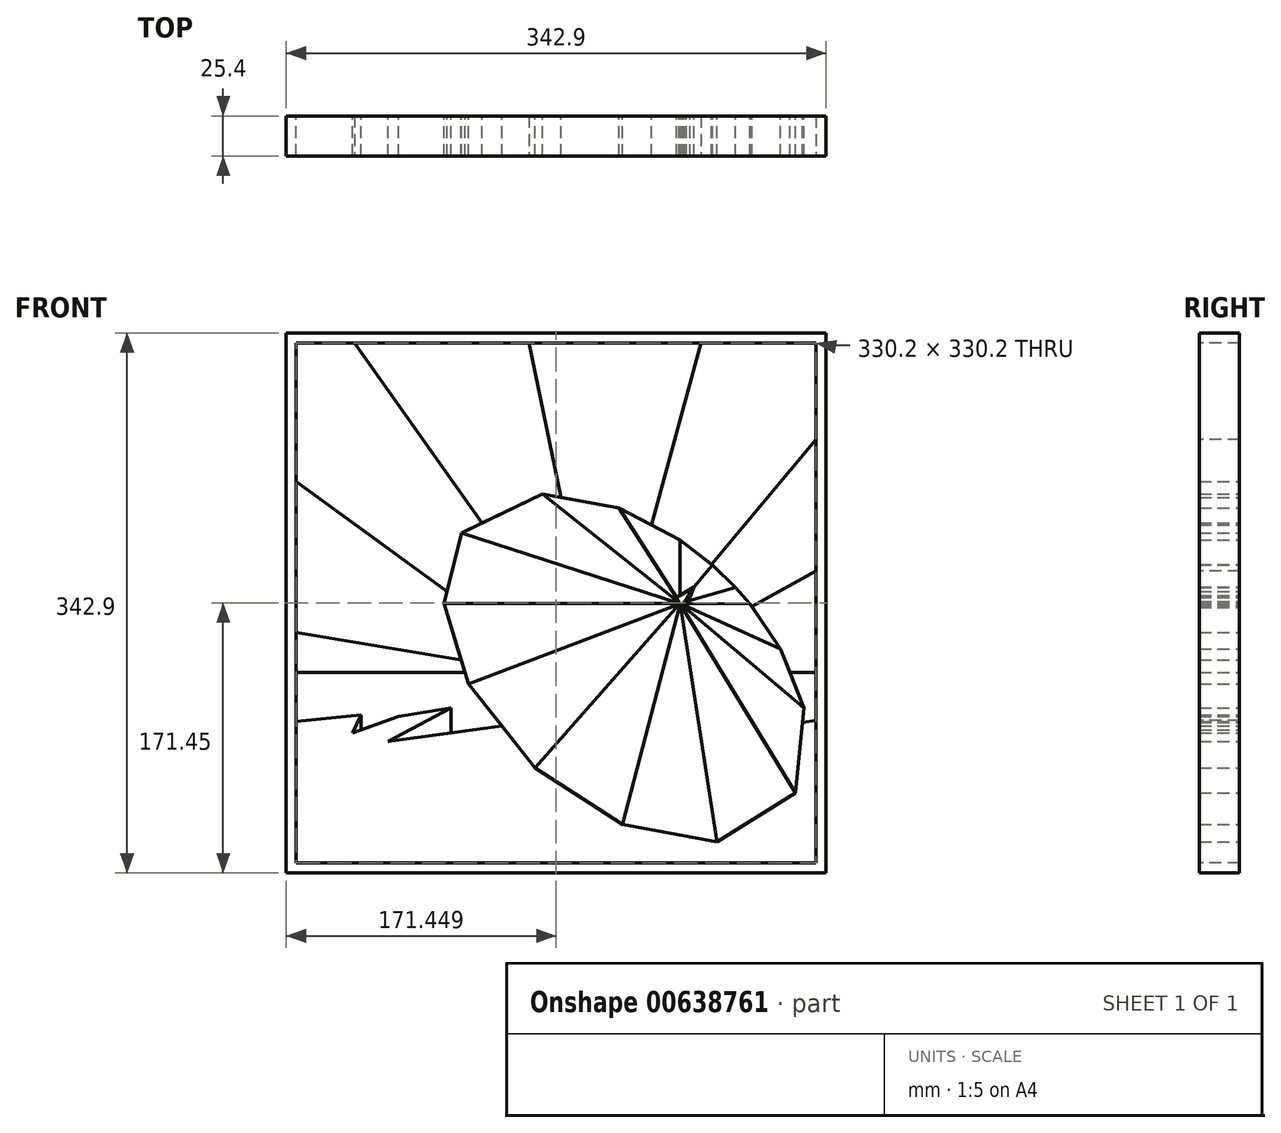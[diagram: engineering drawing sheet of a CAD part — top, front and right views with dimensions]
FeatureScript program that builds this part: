
annotation { "Feature Type Name" : "Feature", "Feature Type Description" : "" }
export const myFeature = defineFeature(function(context is Context, id is Id, definition is map)
    precondition{}
    {
        {
            var Q0;
            Q0=qCreatedBy(makeId("Front.planeOp"),FACE);
            var sketch = newSketch(context, id + "F0", { "sketchPlane" : qUnion([Q0])});
            skLineSegment(sketch, "E0.bottom", {"start": v(-193.2, 254) * mm, "end": v(149.7, 254) * mm});
            skLineSegment(sketch, "E0.top", {"start": v(-193.2, -88.9) * mm, "end": v(149.7, -88.9) * mm});
            skLineSegment(sketch, "E0.left", {"start": v(-193.2, 254) * mm, "end": v(-193.2, -88.9) * mm});
            skLineSegment(sketch, "E0.right", {"start": v(149.7, 254) * mm, "end": v(149.7, -88.9) * mm});
            skPoint(sketch, "E0.middle", {"position": v(0, 0) * mm});
            skLineSegment(sketch, "E1", {"start": v(80.35, -69.06) * mm, "end": v(57.06, 81.1) * mm});
            skLineSegment(sketch, "E2", {"start": v(56.75, 81.7) * mm, "end": v(20.29, -58.17) * mm});
            skLineSegment(sketch, "E3", {"start": v(56.62, 81.93) * mm, "end": v(-35.2, -22.32) * mm});
            skLineSegment(sketch, "E4", {"start": v(56.53, 82.1) * mm, "end": v(-77.42, 31.1) * mm});
            skLineSegment(sketch, "E5", {"start": v(58.15, 80.16) * mm, "end": v(130.28, -38.23) * mm});
            skLineSegment(sketch, "E6", {"start": v(58.72, 80.68) * mm, "end": v(135.54, 15.8) * mm});
            skLineSegment(sketch, "E7", {"start": v(59.17, 81.2) * mm, "end": v(120.65, 53.47) * mm});
            skLineSegment(sketch, "E8", {"start": v(65.8, 92.78) * mm, "end": v(77.44, 106.57) * mm});
            skLineSegment(sketch, "E9", {"start": v(60.02, 82.2) * mm, "end": v(101.38, 81.8) * mm});
            skLineSegment(sketch, "E10", {"start": v(56.16, 82.82) * mm, "end": v(-30.36, 151.77) * mm});
            skLineSegment(sketch, "E11", {"start": v(56.38, 82.4) * mm, "end": v(-81.92, 126.98) * mm});
            skLineSegment(sketch, "E12", {"start": v(54.53, 85.91) * mm, "end": v(17.96, 142.97) * mm});
            skLineSegment(sketch, "E13", {"start": v(56.89, 87.35) * mm, "end": v(56.89, 122.55) * mm});
            skLineSegment(sketch, "E14", {"start": v(61.1, 83.45) * mm, "end": v(92.06, 92.44) * mm});
            skPoint(sketch, "E14.endSnap0", {"position": v(64.87, 92.44) * mm});
            skLineSegment(sketch, "E15", {"start": v(92.06, 92.44) * mm, "end": v(92.06, 92.44) * mm});
            skLineSegment(sketch, "E16", {"start": v(101.38, 81.8) * mm, "end": v(101.38, 81.8) * mm});
            skLineSegment(sketch, "E17", {"start": v(-35.2, -22.32) * mm, "end": v(-35.2, -22.32) * mm});
            skLineSegment(sketch, "E18.bottom", {"start": v(-792.58, 106.28) * mm, "end": v(-449.68, 106.28) * mm});
            skLineSegment(sketch, "E18.top", {"start": v(-792.58, -236.62) * mm, "end": v(-449.68, -236.62) * mm});
            skLineSegment(sketch, "E18.left", {"start": v(-792.58, 106.28) * mm, "end": v(-792.58, -236.62) * mm});
            skLineSegment(sketch, "E18.right", {"start": v(-449.68, 106.28) * mm, "end": v(-449.68, -236.62) * mm});
            skPoint(sketch, "E18.middle", {"position": v(-621.13, -147.72) * mm});
            skEllipse(sketch, "E19", {"center": v(-604.47, -108.06) * mm, "majorRadius": 135.13 * mm, "minorRadius": 85.6 * mm, "majorAxis": v(0.74, -0.67), "construction": true});
            skLineSegment(sketch, "E20", {"start": v(-538.84, -217.22) * mm, "end": v(-568.58, -63.1) * mm});
            skLineSegment(sketch, "E21", {"start": v(-568.58, -63.1) * mm, "end": v(-597.53, -210.85) * mm});
            skLineSegment(sketch, "E22", {"start": v(-568.58, -63.1) * mm, "end": v(-661.88, -171.55) * mm});
            skLineSegment(sketch, "E23", {"start": v(-568.58, -63.1) * mm, "end": v(-704.54, -117.27) * mm});
            skLineSegment(sketch, "E24", {"start": v(-568.58, -63.1) * mm, "end": v(-719.04, -48.6) * mm});
            skLineSegment(sketch, "E25", {"start": v(-568.58, -63.1) * mm, "end": v(-685.76, -3.78) * mm});
            skLineSegment(sketch, "E26", {"start": v(-568.58, -63.1) * mm, "end": v(-629.1, -0.19) * mm});
            skLineSegment(sketch, "E27", {"start": v(-568.58, -63.1) * mm, "end": v(-493.58, -181.32) * mm});
            skLineSegment(sketch, "E28", {"start": v(-568.58, -63.1) * mm, "end": v(-493.3, -126.16) * mm});
            skLineSegment(sketch, "E29", {"start": v(-568.58, -63.1) * mm, "end": v(-511.11, -87.15) * mm});
            skLineSegment(sketch, "E30", {"start": v(-568.58, -63.1) * mm, "end": v(-550.5, -41.52) * mm});
            skLineSegment(sketch, "E31", {"start": v(-568.58, -63.1) * mm, "end": v(-543.93, -47.46) * mm});
            skLineSegment(sketch, "E32", {"start": v(-568.58, -63.1) * mm, "end": v(-519.08, -75.43) * mm});
            skLineSegment(sketch, "E33", {"start": v(-568.58, -63.1) * mm, "end": v(-500.79, -106.18) * mm});
            skLineSegment(sketch, "E34", {"start": v(-568.58, -63.1) * mm, "end": v(-488.96, -154.6) * mm});
            skLineSegment(sketch, "E35", {"start": v(-568.58, -63.1) * mm, "end": v(-657.04, 2.54) * mm});
            skLineSegment(sketch, "E36", {"start": v(-568.58, -63.1) * mm, "end": v(-708.59, -22.25) * mm});
            skLineSegment(sketch, "E37", {"start": v(-568.58, -63.1) * mm, "end": v(-717.58, -82.24) * mm});
            skLineSegment(sketch, "E38", {"start": v(-568.58, -63.1) * mm, "end": v(-684.44, -147.72) * mm});
            skLineSegment(sketch, "E39", {"start": v(-568.58, -63.1) * mm, "end": v(-634.18, -192.72) * mm});
            skLineSegment(sketch, "E40", {"start": v(-568.58, -63.1) * mm, "end": v(-568.58, -217.87) * mm});
            skLineSegment(sketch, "E41", {"start": v(-568.58, -63.1) * mm, "end": v(-511.8, -205.61) * mm});
            skLineSegment(sketch, "E42", {"start": v(-568.58, -63.1) * mm, "end": v(-599.26, -10.15) * mm});
            skLineSegment(sketch, "E43", {"start": v(-568.58, -63.1) * mm, "end": v(-581.85, -19.08) * mm});
            skLineSegment(sketch, "E44", {"start": v(-568.58, -63.1) * mm, "end": v(-568.58, -27.51) * mm});
            skLineSegment(sketch, "E45", {"start": v(-568.58, -63.1) * mm, "end": v(-560.02, -33.76) * mm});
            skLineSegment(sketch, "E46", {"start": v(-568.58, -63.1) * mm, "end": v(-536.04, -55.28) * mm});
            skPoint(sketch, "E46.endSnap0", {"position": v(-556.25, -55.28) * mm});
            skLineSegment(sketch, "E47", {"start": v(-568.58, -63.1) * mm, "end": v(-528.93, -63.1) * mm});
            skLineSegment(sketch, "E48", {"start": v(-568.58, -63.1) * mm, "end": v(-604.47, -108.06) * mm, "construction": true});
            skLineSegment(sketch, "E49", {"start": v(-719.04, -48.6) * mm, "end": v(-708.59, -22.25) * mm});
            skLineSegment(sketch, "E50", {"start": v(-708.59, -22.25) * mm, "end": v(-685.76, -3.78) * mm});
            skLineSegment(sketch, "E51", {"start": v(-685.76, -3.78) * mm, "end": v(-657.04, 2.54) * mm});
            skLineSegment(sketch, "E52", {"start": v(-657.04, 2.54) * mm, "end": v(-629.1, -0.19) * mm});
            skLineSegment(sketch, "E53", {"start": v(-629.1, -0.19) * mm, "end": v(-599.26, -10.15) * mm});
            skLineSegment(sketch, "E54", {"start": v(-599.26, -10.15) * mm, "end": v(-581.85, -19.08) * mm});
            skLineSegment(sketch, "E55", {"start": v(-581.85, -19.08) * mm, "end": v(-568.58, -27.51) * mm});
            skLineSegment(sketch, "E56", {"start": v(-568.58, -27.51) * mm, "end": v(-560.02, -33.76) * mm});
            skLineSegment(sketch, "E57", {"start": v(-560.02, -33.76) * mm, "end": v(-550.5, -41.52) * mm});
            skLineSegment(sketch, "E58", {"start": v(-550.5, -41.52) * mm, "end": v(-543.93, -47.46) * mm});
            skLineSegment(sketch, "E59", {"start": v(-543.93, -47.46) * mm, "end": v(-536.04, -55.28) * mm});
            skLineSegment(sketch, "E60", {"start": v(-536.04, -55.28) * mm, "end": v(-528.93, -63.1) * mm});
            skLineSegment(sketch, "E61", {"start": v(-528.93, -63.1) * mm, "end": v(-519.08, -75.43) * mm});
            skLineSegment(sketch, "E62", {"start": v(-519.08, -75.43) * mm, "end": v(-511.11, -87.15) * mm});
            skLineSegment(sketch, "E63", {"start": v(-511.11, -87.15) * mm, "end": v(-500.79, -106.18) * mm});
            skLineSegment(sketch, "E64", {"start": v(-500.79, -106.18) * mm, "end": v(-493.3, -126.16) * mm});
            skLineSegment(sketch, "E65", {"start": v(-493.3, -126.16) * mm, "end": v(-488.96, -154.6) * mm});
            skLineSegment(sketch, "E66", {"start": v(-488.96, -154.6) * mm, "end": v(-493.58, -181.32) * mm});
            skLineSegment(sketch, "E67", {"start": v(-493.58, -181.32) * mm, "end": v(-511.8, -205.61) * mm});
            skLineSegment(sketch, "E68", {"start": v(-511.8, -205.61) * mm, "end": v(-538.84, -217.22) * mm});
            skLineSegment(sketch, "E69", {"start": v(-538.84, -217.22) * mm, "end": v(-568.58, -217.87) * mm});
            skLineSegment(sketch, "E70", {"start": v(-568.58, -217.87) * mm, "end": v(-597.53, -210.85) * mm});
            skLineSegment(sketch, "E71", {"start": v(-597.53, -210.85) * mm, "end": v(-634.18, -192.72) * mm});
            skLineSegment(sketch, "E72", {"start": v(-634.18, -192.72) * mm, "end": v(-661.88, -171.55) * mm});
            skLineSegment(sketch, "E73", {"start": v(-661.88, -171.55) * mm, "end": v(-684.44, -147.72) * mm});
            skLineSegment(sketch, "E74", {"start": v(-684.44, -147.72) * mm, "end": v(-704.54, -117.27) * mm});
            skLineSegment(sketch, "E75", {"start": v(-704.54, -117.27) * mm, "end": v(-717.58, -82.24) * mm});
            skLineSegment(sketch, "E76", {"start": v(-717.58, -82.24) * mm, "end": v(-719.04, -48.6) * mm});
            skLineSegment(sketch, "E77", {"start": v(-657.7, -174.75) * mm, "end": v(-657.93, -175.04) * mm});
            skLineSegment(sketch, "E78.0", {"start": v(-658.96, -173.78) * mm, "end": v(-679.18, -199.12) * mm});
            skLineSegment(sketch, "E79.0", {"start": v(-656.43, -175.71) * mm, "end": v(-676.7, -201.1) * mm});
            skLineSegment(sketch, "E80", {"start": v(-792.58, -50.28) * mm, "end": v(-718.96, -50.28) * mm});
            skLineSegment(sketch, "E81", {"start": v(-718.96, -50.28) * mm, "end": v(-541.08, -50.28) * mm, "construction": true});
            skLineSegment(sketch, "E82", {"start": v(-541.08, -50.28) * mm, "end": v(-449.68, -50.28) * mm});
            skLineSegment(sketch, "E83", {"start": v(-679.18, -199.12) * mm, "end": v(-676.7, -201.1) * mm});
            skLineSegment(sketch, "E84", {"start": v(56.46, 82.23) * mm, "end": v(-93.1, 82.23) * mm});
            skLineSegment(sketch, "E85", {"start": v(54.53, 85.91) * mm, "end": v(65.8, 92.78) * mm});
            skLineSegment(sketch, "E86", {"start": v(54.53, 85.91) * mm, "end": v(57.83, 79.63) * mm});
            skLineSegment(sketch, "E87", {"start": v(57.83, 79.63) * mm, "end": v(65.8, 92.78) * mm});
            skLineSegment(sketch, "E88", {"start": v(57.83, 79.63) * mm, "end": v(63.2, 85.91) * mm});
            skLineSegment(sketch, "E89", {"start": v(63.2, 85.91) * mm, "end": v(65.8, 92.78) * mm});
            skPoint(sketch, "E90.orphan", {"position": v(56.89, 82.23) * mm});
            skLineSegment(sketch, "E91", {"start": v(-30.36, 151.77) * mm, "end": v(-81.92, 126.98) * mm});
            skLineSegment(sketch, "E92", {"start": v(-81.92, 126.98) * mm, "end": v(-93.1, 82.23) * mm});
            skLineSegment(sketch, "E93", {"start": v(-93.1, 82.23) * mm, "end": v(-77.42, 31.1) * mm});
            skLineSegment(sketch, "E94", {"start": v(-77.42, 31.1) * mm, "end": v(-35.2, -22.32) * mm});
            skLineSegment(sketch, "E95", {"start": v(-35.2, -22.32) * mm, "end": v(20.29, -58.17) * mm});
            skLineSegment(sketch, "E96", {"start": v(20.29, -58.17) * mm, "end": v(80.35, -69.06) * mm});
            skLineSegment(sketch, "E97", {"start": v(130.28, -38.23) * mm, "end": v(80.35, -69.06) * mm});
            skLineSegment(sketch, "E98", {"start": v(130.28, -38.23) * mm, "end": v(135.54, 15.8) * mm});
            skLineSegment(sketch, "E99", {"start": v(135.54, 15.8) * mm, "end": v(120.65, 53.47) * mm});
            skLineSegment(sketch, "E100", {"start": v(101.38, 81.8) * mm, "end": v(120.65, 53.47) * mm});
            skLineSegment(sketch, "E101", {"start": v(92.06, 92.44) * mm, "end": v(101.38, 81.8) * mm});
            skLineSegment(sketch, "E102", {"start": v(77.44, 106.57) * mm, "end": v(92.06, 92.44) * mm});
            skLineSegment(sketch, "E103", {"start": v(-30.36, 151.77) * mm, "end": v(17.96, 142.97) * mm});
            skLineSegment(sketch, "E104", {"start": v(17.96, 142.97) * mm, "end": v(56.89, 122.55) * mm});
            skLineSegment(sketch, "E105", {"start": v(56.89, 122.55) * mm, "end": v(77.44, 106.57) * mm});
            skLineSegment(sketch, "E106", {"start": v(-121.9, 10.45) * mm, "end": v(-151.05, 0) * mm});
            skLineSegment(sketch, "E107", {"start": v(-151.05, 0) * mm, "end": v(-145.58, 11.5) * mm});
            skLineSegment(sketch, "E108", {"start": v(-121.9, 10.45) * mm, "end": v(-88.6, 15.97) * mm});
            skLineSegment(sketch, "E109", {"start": v(-145.58, 11.5) * mm, "end": v(-145.58, 1.96) * mm});
            skLineSegment(sketch, "E110", {"start": v(-88.6, 15.97) * mm, "end": v(-128.67, -5.45) * mm});
            skLineSegment(sketch, "E111", {"start": v(-128.67, -5.45) * mm, "end": v(-56.31, 4.39) * mm});
            skLineSegment(sketch, "E112", {"start": v(-88.6, 15.97) * mm, "end": v(-88.6, 0) * mm});
            skLineSegment(sketch, "E113", {"start": v(-145.58, 11.5) * mm, "end": v(-193.2, 6.73) * mm});
            skPoint(sketch, "E113.endSnap0", {"position": v(-145.58, 6.73) * mm});
            skPoint(sketch, "E114.endSnap0", {"position": v(132.91, -11.21) * mm});
            skLineSegment(sketch, "E115", {"start": v(149.7, 8.76) * mm, "end": v(149.46, 8.7) * mm});
            skLineSegment(sketch, "E116", {"start": v(-193.2, 38.5) * mm, "end": v(-79.69, 38.5) * mm});
            skLineSegment(sketch, "E117", {"start": v(149.7, 38.5) * mm, "end": v(126.57, 38.5) * mm});
            skLineSegment(sketch, "E118", {"start": v(134.66, 6.7) * mm, "end": v(149.46, 8.7) * mm});
            skLineSegment(sketch, "E119", {"start": v(-91.17, 89.95) * mm, "end": v(-193.2, 164.23) * mm});
            skLineSegment(sketch, "E120.trimOffspring", {"start": v(-82.08, 46.3) * mm, "end": v(-193.2, 65.07) * mm});
            skLineSegment(sketch, "E121.trimOffspring", {"start": v(-68.82, 133.27) * mm, "end": v(-154.33, 254) * mm});
            skLineSegment(sketch, "E122.trimOffspring", {"start": v(-18.82, 149.66) * mm, "end": v(-40.22, 254) * mm});
            skLineSegment(sketch, "E123.trimOffspring", {"start": v(38.79, 132.04) * mm, "end": v(71.85, 254) * mm});
            skPoint(sketch, "E124.start.orphan", {"position": v(-40.31, 38.5) * mm});
            skLineSegment(sketch, "E125.trimOffspring", {"start": v(102.44, 80.24) * mm, "end": v(149.7, 106.5) * mm});
            skLineSegment(sketch, "E126.trimOffspring", {"start": v(76.68, 107.16) * mm, "end": v(149.7, 194.12) * mm});
            skLineSegment(sketch, "E127.bottom", {"start": v(443.16, -49.15) * mm, "end": v(786.06, -49.15) * mm});
            skLineSegment(sketch, "E127.top", {"start": v(443.16, -392.05) * mm, "end": v(786.06, -392.05) * mm});
            skLineSegment(sketch, "E127.left", {"start": v(443.16, -49.15) * mm, "end": v(443.16, -392.05) * mm});
            skLineSegment(sketch, "E127.right", {"start": v(786.06, -49.15) * mm, "end": v(786.06, -392.05) * mm});
            skPoint(sketch, "E127.middle", {"position": v(636.36, -303.15) * mm});
            skLineSegment(sketch, "E128", {"start": v(716.71, -372.2) * mm, "end": v(693.42, -222.06) * mm});
            skLineSegment(sketch, "E129", {"start": v(693.1, -221.45) * mm, "end": v(656.64, -361.32) * mm});
            skLineSegment(sketch, "E130", {"start": v(692.98, -221.21) * mm, "end": v(601.15, -325.47) * mm});
            skLineSegment(sketch, "E131", {"start": v(692.9, -221.05) * mm, "end": v(558.94, -272.05) * mm});
            skLineSegment(sketch, "E132", {"start": v(694.5, -222.98) * mm, "end": v(766.64, -341.38) * mm});
            skLineSegment(sketch, "E133", {"start": v(695.08, -222.46) * mm, "end": v(771.92, -287.15) * mm});
            skLineSegment(sketch, "E134", {"start": v(695.52, -221.93) * mm, "end": v(756.85, -249.45) * mm});
            skLineSegment(sketch, "E135", {"start": v(702.18, -210.3) * mm, "end": v(713.76, -196.54) * mm});
            skLineSegment(sketch, "E136", {"start": v(696.36, -220.94) * mm, "end": v(737.74, -221.35) * mm});
            skLineSegment(sketch, "E137", {"start": v(692.51, -220.33) * mm, "end": v(606, -151.38) * mm});
            skLineSegment(sketch, "E138", {"start": v(692.73, -220.75) * mm, "end": v(554.44, -176.17) * mm});
            skLineSegment(sketch, "E139", {"start": v(690.89, -217.23) * mm, "end": v(654.31, -160.18) * mm});
            skLineSegment(sketch, "E140", {"start": v(693.24, -215.8) * mm, "end": v(693.24, -180.6) * mm});
            skLineSegment(sketch, "E141", {"start": v(697.4, -219.7) * mm, "end": v(728.42, -210.7) * mm});
            skPoint(sketch, "E141.endSnap0", {"position": v(701.23, -210.7) * mm});
            skLineSegment(sketch, "E142", {"start": v(728.42, -210.7) * mm, "end": v(728.42, -210.7) * mm});
            skLineSegment(sketch, "E143", {"start": v(737.74, -221.35) * mm, "end": v(737.74, -221.35) * mm});
            skLineSegment(sketch, "E144", {"start": v(756.85, -249.45) * mm, "end": v(758.04, -251.63) * mm});
            skLineSegment(sketch, "E145", {"start": v(601.15, -325.47) * mm, "end": v(601.15, -325.47) * mm});
            skLineSegment(sketch, "E146", {"start": v(603.31, -327.4) * mm, "end": v(601.53, -329.5) * mm});
            skLineSegment(sketch, "E147.0", {"start": v(601.32, -327.29) * mm, "end": v(578.3, -354.55) * mm});
            skLineSegment(sketch, "E148.0", {"start": v(601.74, -331.72) * mm, "end": v(580.78, -356.53) * mm});
            skLineSegment(sketch, "E149", {"start": v(578.3, -354.55) * mm, "end": v(580.78, -356.53) * mm});
            skLineSegment(sketch, "E150", {"start": v(692.82, -220.91) * mm, "end": v(543.25, -220.91) * mm});
            skLineSegment(sketch, "E151", {"start": v(690.89, -217.23) * mm, "end": v(702.15, -210.37) * mm});
            skLineSegment(sketch, "E152", {"start": v(690.89, -217.23) * mm, "end": v(694.19, -223.51) * mm});
            skLineSegment(sketch, "E153", {"start": v(694.19, -223.51) * mm, "end": v(702.15, -210.37) * mm});
            skLineSegment(sketch, "E154", {"start": v(694.19, -223.51) * mm, "end": v(699.5, -217.23) * mm});
            skLineSegment(sketch, "E155", {"start": v(699.5, -217.23) * mm, "end": v(702.15, -210.37) * mm});
            skPoint(sketch, "E156.orphan", {"position": v(693.24, -220.91) * mm});
            skLineSegment(sketch, "E157", {"start": v(606, -151.38) * mm, "end": v(554.44, -176.17) * mm});
            skLineSegment(sketch, "E158", {"start": v(554.44, -176.17) * mm, "end": v(543.25, -220.91) * mm});
            skLineSegment(sketch, "E159", {"start": v(543.25, -220.91) * mm, "end": v(558.94, -272.05) * mm});
            skLineSegment(sketch, "E160", {"start": v(558.94, -272.05) * mm, "end": v(601.15, -325.47) * mm});
            skLineSegment(sketch, "E161", {"start": v(601.15, -325.47) * mm, "end": v(656.64, -361.32) * mm});
            skLineSegment(sketch, "E162", {"start": v(656.64, -361.32) * mm, "end": v(716.71, -372.2) * mm});
            skLineSegment(sketch, "E163", {"start": v(766.64, -341.38) * mm, "end": v(716.71, -372.2) * mm});
            skLineSegment(sketch, "E164", {"start": v(766.64, -341.38) * mm, "end": v(771.92, -287.15) * mm});
            skLineSegment(sketch, "E165", {"start": v(771.92, -287.15) * mm, "end": v(756.85, -249.45) * mm});
            skLineSegment(sketch, "E166", {"start": v(737.74, -221.35) * mm, "end": v(756.85, -249.45) * mm});
            skLineSegment(sketch, "E167", {"start": v(728.42, -210.7) * mm, "end": v(737.74, -221.35) * mm});
            skLineSegment(sketch, "E168", {"start": v(713.76, -196.54) * mm, "end": v(728.42, -210.7) * mm});
            skLineSegment(sketch, "E169", {"start": v(606, -151.38) * mm, "end": v(654.31, -160.18) * mm});
            skLineSegment(sketch, "E170", {"start": v(654.31, -160.18) * mm, "end": v(693.24, -180.6) * mm});
            skLineSegment(sketch, "E171", {"start": v(693.24, -180.6) * mm, "end": v(713.76, -196.54) * mm});
            skLineSegment(sketch, "E172", {"start": v(514.45, -292.7) * mm, "end": v(485.3, -303.15) * mm});
            skLineSegment(sketch, "E173", {"start": v(485.3, -303.15) * mm, "end": v(490.78, -291.65) * mm});
            skLineSegment(sketch, "E174", {"start": v(514.45, -292.7) * mm, "end": v(548.76, -287.02) * mm});
            skLineSegment(sketch, "E175", {"start": v(490.78, -291.65) * mm, "end": v(490.78, -301.19) * mm});
            skLineSegment(sketch, "E176", {"start": v(548.76, -287.02) * mm, "end": v(507.88, -309.95) * mm});
            skLineSegment(sketch, "E177", {"start": v(507.88, -309.95) * mm, "end": v(580.05, -298.76) * mm});
            skLineSegment(sketch, "E178", {"start": v(548.76, -287.02) * mm, "end": v(548.76, -303.15) * mm});
            skLineSegment(sketch, "E179", {"start": v(490.78, -291.65) * mm, "end": v(443.16, -296.42) * mm});
            skPoint(sketch, "E179.endSnap0", {"position": v(490.78, -296.42) * mm});
            skPoint(sketch, "E180.endSnap0", {"position": v(769.28, -314.26) * mm});
            skLineSegment(sketch, "E181", {"start": v(786.06, -294.39) * mm, "end": v(785.82, -294.44) * mm});
            skLineSegment(sketch, "E182", {"start": v(443.16, -263.89) * mm, "end": v(555.39, -263.89) * mm});
            skLineSegment(sketch, "E183", {"start": v(786.06, -263.89) * mm, "end": v(762.96, -263.89) * mm});
            skLineSegment(sketch, "E184", {"start": v(771.02, -296.44) * mm, "end": v(785.82, -294.44) * mm});
            skLineSegment(sketch, "E185", {"start": v(691.58, -221.55) * mm, "end": v(692.55, -220.4) * mm});
            skPoint(sketch, "E186.start.orphan", {"position": v(596.04, -263.89) * mm});
            skLineSegment(sketch, "E187.bottom", {"start": v(-369.84, -367.12) * mm, "end": v(-26.94, -367.12) * mm});
            skLineSegment(sketch, "E187.top", {"start": v(-369.84, -710.02) * mm, "end": v(-26.94, -710.02) * mm});
            skLineSegment(sketch, "E187.left", {"start": v(-369.84, -367.12) * mm, "end": v(-369.84, -710.02) * mm});
            skLineSegment(sketch, "E187.right", {"start": v(-26.94, -367.12) * mm, "end": v(-26.94, -710.02) * mm});
            skLineSegment(sketch, "E188", {"start": v(-96.3, -690.18) * mm, "end": v(-119.58, -540.03) * mm});
            skLineSegment(sketch, "E189", {"start": v(-119.9, -539.43) * mm, "end": v(-156.36, -679.3) * mm});
            skLineSegment(sketch, "E190", {"start": v(-120.02, -539.2) * mm, "end": v(-211.85, -643.45) * mm});
            skLineSegment(sketch, "E191", {"start": v(-120.1, -539.02) * mm, "end": v(-254.06, -590.03) * mm});
            skLineSegment(sketch, "E192", {"start": v(-118.5, -540.96) * mm, "end": v(-46.36, -659.35) * mm});
            skLineSegment(sketch, "E193", {"start": v(-117.92, -540.43) * mm, "end": v(-41.08, -605.13) * mm});
            skLineSegment(sketch, "E194", {"start": v(-117.48, -539.91) * mm, "end": v(-56.15, -567.42) * mm});
            skLineSegment(sketch, "E195", {"start": v(-110.82, -528.28) * mm, "end": v(-99.24, -514.52) * mm});
            skLineSegment(sketch, "E196", {"start": v(-116.64, -538.92) * mm, "end": v(-75.26, -539.32) * mm});
            skLineSegment(sketch, "E197", {"start": v(-120.49, -538.3) * mm, "end": v(-207, -469.36) * mm});
            skLineSegment(sketch, "E198", {"start": v(-120.27, -538.73) * mm, "end": v(-258.56, -494.15) * mm});
            skLineSegment(sketch, "E199", {"start": v(-122.12, -535.2) * mm, "end": v(-158.69, -478.15) * mm});
            skLineSegment(sketch, "E200", {"start": v(-119.76, -533.77) * mm, "end": v(-119.76, -498.58) * mm});
            skLineSegment(sketch, "E201", {"start": v(-115.6, -537.68) * mm, "end": v(-84.58, -528.68) * mm});
            skLineSegment(sketch, "E202", {"start": v(-84.58, -528.68) * mm, "end": v(-84.58, -528.68) * mm});
            skLineSegment(sketch, "E203", {"start": v(-75.26, -539.32) * mm, "end": v(-75.26, -539.32) * mm});
            skLineSegment(sketch, "E204", {"start": v(-211.85, -643.45) * mm, "end": v(-211.85, -643.45) * mm});
            skLineSegment(sketch, "E205", {"start": v(-120.18, -538.9) * mm, "end": v(-269.75, -538.9) * mm});
            skLineSegment(sketch, "E206", {"start": v(-122.12, -535.2) * mm, "end": v(-110.85, -528.35) * mm});
            skLineSegment(sketch, "E207", {"start": v(-122.12, -535.2) * mm, "end": v(-118.81, -541.49) * mm});
            skLineSegment(sketch, "E208", {"start": v(-118.81, -541.49) * mm, "end": v(-110.85, -528.35) * mm});
            skLineSegment(sketch, "E209", {"start": v(-118.81, -541.49) * mm, "end": v(-113.51, -535.2) * mm});
            skLineSegment(sketch, "E210", {"start": v(-113.51, -535.2) * mm, "end": v(-110.85, -528.35) * mm});
            skLineSegment(sketch, "E211", {"start": v(-207, -469.36) * mm, "end": v(-258.56, -494.15) * mm});
            skLineSegment(sketch, "E212", {"start": v(-258.56, -494.15) * mm, "end": v(-269.75, -538.9) * mm});
            skLineSegment(sketch, "E213", {"start": v(-269.75, -538.9) * mm, "end": v(-254.06, -590.03) * mm});
            skLineSegment(sketch, "E214", {"start": v(-254.06, -590.03) * mm, "end": v(-211.85, -643.45) * mm});
            skLineSegment(sketch, "E215", {"start": v(-211.85, -643.45) * mm, "end": v(-156.36, -679.3) * mm});
            skLineSegment(sketch, "E216", {"start": v(-156.36, -679.3) * mm, "end": v(-96.3, -690.18) * mm});
            skLineSegment(sketch, "E217", {"start": v(-46.36, -659.35) * mm, "end": v(-96.3, -690.18) * mm});
            skLineSegment(sketch, "E218", {"start": v(-46.36, -659.35) * mm, "end": v(-41.08, -605.13) * mm});
            skLineSegment(sketch, "E219", {"start": v(-41.08, -605.13) * mm, "end": v(-56.15, -567.42) * mm});
            skLineSegment(sketch, "E220", {"start": v(-75.26, -539.32) * mm, "end": v(-56.15, -567.42) * mm});
            skLineSegment(sketch, "E221", {"start": v(-84.58, -528.68) * mm, "end": v(-75.26, -539.32) * mm});
            skLineSegment(sketch, "E222", {"start": v(-99.24, -514.52) * mm, "end": v(-84.58, -528.68) * mm});
            skLineSegment(sketch, "E223", {"start": v(-207, -469.36) * mm, "end": v(-158.69, -478.15) * mm});
            skLineSegment(sketch, "E224", {"start": v(-158.69, -478.15) * mm, "end": v(-119.76, -498.58) * mm});
            skLineSegment(sketch, "E225", {"start": v(-119.76, -498.58) * mm, "end": v(-99.24, -514.52) * mm});
            skLineSegment(sketch, "E226", {"start": v(-26.94, -612.37) * mm, "end": v(-27.18, -612.42) * mm});
            skLineSegment(sketch, "E227", {"start": v(-369.84, -521.6) * mm, "end": v(-265.42, -521.6) * mm});
            skLineSegment(sketch, "E228", {"start": v(-26.94, -521.6) * mm, "end": v(-91.91, -521.6) * mm});
            skLineSegment(sketch, "E229", {"start": v(-121.42, -539.53) * mm, "end": v(-120.45, -538.37) * mm});
            skLineSegment(sketch, "E230.bottom", {"start": v(426.95, -620.52) * mm, "end": v(769.85, -620.52) * mm});
            skLineSegment(sketch, "E230.top", {"start": v(426.95, -963.42) * mm, "end": v(769.85, -963.42) * mm});
            skLineSegment(sketch, "E230.left", {"start": v(426.95, -620.52) * mm, "end": v(426.95, -963.42) * mm});
            skLineSegment(sketch, "E230.right", {"start": v(769.85, -620.52) * mm, "end": v(769.85, -963.42) * mm});
            skPoint(sketch, "E230.middle", {"position": v(620.15, -874.52) * mm});
            skLineSegment(sketch, "E231", {"start": v(700.5, -943.58) * mm, "end": v(677.21, -793.43) * mm});
            skLineSegment(sketch, "E232", {"start": v(676.9, -792.83) * mm, "end": v(640.44, -932.7) * mm});
            skLineSegment(sketch, "E233", {"start": v(676.77, -792.6) * mm, "end": v(584.94, -896.85) * mm});
            skLineSegment(sketch, "E234", {"start": v(676.68, -792.42) * mm, "end": v(542.73, -843.43) * mm});
            skLineSegment(sketch, "E235", {"start": v(678.3, -794.36) * mm, "end": v(750.43, -912.75) * mm});
            skLineSegment(sketch, "E236", {"start": v(678.87, -793.83) * mm, "end": v(755.71, -858.53) * mm});
            skLineSegment(sketch, "E237", {"start": v(679.31, -793.31) * mm, "end": v(740.64, -820.82) * mm});
            skLineSegment(sketch, "E238", {"start": v(685.97, -781.68) * mm, "end": v(697.55, -767.92) * mm});
            skLineSegment(sketch, "E239", {"start": v(680.15, -792.32) * mm, "end": v(721.53, -792.72) * mm});
            skLineSegment(sketch, "E240", {"start": v(676.3, -791.7) * mm, "end": v(589.78, -722.76) * mm});
            skLineSegment(sketch, "E241", {"start": v(676.52, -792.12) * mm, "end": v(538.23, -747.55) * mm});
            skLineSegment(sketch, "E242", {"start": v(674.68, -788.6) * mm, "end": v(638.1, -731.55) * mm});
            skLineSegment(sketch, "E243", {"start": v(677.03, -787.17) * mm, "end": v(677.03, -751.98) * mm});
            skLineSegment(sketch, "E244", {"start": v(681.2, -791.08) * mm, "end": v(712.2, -782.08) * mm});
            skPoint(sketch, "E244.endSnap0", {"position": v(685.02, -782.08) * mm});
            skLineSegment(sketch, "E245", {"start": v(712.2, -782.08) * mm, "end": v(712.2, -782.08) * mm});
            skLineSegment(sketch, "E246", {"start": v(721.53, -792.72) * mm, "end": v(721.53, -792.72) * mm});
            skLineSegment(sketch, "E247", {"start": v(740.64, -820.82) * mm, "end": v(741.83, -823) * mm});
            skLineSegment(sketch, "E248", {"start": v(584.94, -896.85) * mm, "end": v(584.94, -896.85) * mm});
            skLineSegment(sketch, "E249", {"start": v(587.77, -898.67) * mm, "end": v(587.44, -899.06) * mm});
            skLineSegment(sketch, "E250.0", {"start": v(586.43, -897.8) * mm, "end": v(574.69, -911.74) * mm});
            skLineSegment(sketch, "E251.0", {"start": v(589.12, -899.54) * mm, "end": v(577.37, -913.48) * mm});
            skLineSegment(sketch, "E252", {"start": v(574.69, -911.74) * mm, "end": v(577.37, -913.48) * mm});
            skLineSegment(sketch, "E253", {"start": v(676.61, -792.29) * mm, "end": v(527.05, -792.29) * mm});
            skLineSegment(sketch, "E254", {"start": v(674.68, -788.6) * mm, "end": v(685.94, -781.75) * mm});
            skLineSegment(sketch, "E255", {"start": v(674.68, -788.6) * mm, "end": v(677.98, -794.89) * mm});
            skLineSegment(sketch, "E256", {"start": v(677.98, -794.89) * mm, "end": v(685.94, -781.75) * mm});
            skLineSegment(sketch, "E257", {"start": v(677.98, -794.89) * mm, "end": v(683.28, -788.6) * mm});
            skLineSegment(sketch, "E258", {"start": v(683.28, -788.6) * mm, "end": v(685.94, -781.75) * mm});
            skPoint(sketch, "E259.orphan", {"position": v(677.03, -792.29) * mm});
            skLineSegment(sketch, "E260", {"start": v(589.78, -722.76) * mm, "end": v(538.23, -747.55) * mm});
            skLineSegment(sketch, "E261", {"start": v(538.23, -747.55) * mm, "end": v(527.05, -792.29) * mm});
            skLineSegment(sketch, "E262", {"start": v(527.05, -792.29) * mm, "end": v(542.73, -843.43) * mm});
            skLineSegment(sketch, "E263", {"start": v(542.73, -843.43) * mm, "end": v(584.94, -896.85) * mm});
            skLineSegment(sketch, "E264", {"start": v(584.94, -896.85) * mm, "end": v(640.44, -932.7) * mm});
            skLineSegment(sketch, "E265", {"start": v(640.44, -932.7) * mm, "end": v(700.5, -943.58) * mm});
            skLineSegment(sketch, "E266", {"start": v(750.43, -912.75) * mm, "end": v(700.5, -943.58) * mm});
            skLineSegment(sketch, "E267", {"start": v(750.43, -912.75) * mm, "end": v(755.71, -858.53) * mm});
            skLineSegment(sketch, "E268", {"start": v(755.71, -858.53) * mm, "end": v(740.64, -820.82) * mm});
            skLineSegment(sketch, "E269", {"start": v(721.53, -792.72) * mm, "end": v(740.64, -820.82) * mm});
            skLineSegment(sketch, "E270", {"start": v(712.2, -782.08) * mm, "end": v(721.53, -792.72) * mm});
            skLineSegment(sketch, "E271", {"start": v(697.55, -767.92) * mm, "end": v(712.2, -782.08) * mm});
            skLineSegment(sketch, "E272", {"start": v(589.78, -722.76) * mm, "end": v(638.1, -731.55) * mm});
            skLineSegment(sketch, "E273", {"start": v(638.1, -731.55) * mm, "end": v(677.03, -751.98) * mm});
            skLineSegment(sketch, "E274", {"start": v(677.03, -751.98) * mm, "end": v(697.55, -767.92) * mm});
            skLineSegment(sketch, "E275", {"start": v(498.24, -864.08) * mm, "end": v(469.1, -874.52) * mm});
            skLineSegment(sketch, "E276", {"start": v(469.1, -874.52) * mm, "end": v(474.57, -863.03) * mm});
            skLineSegment(sketch, "E277", {"start": v(498.24, -864.08) * mm, "end": v(532.55, -858.4) * mm});
            skLineSegment(sketch, "E278", {"start": v(474.57, -863.03) * mm, "end": v(474.57, -872.56) * mm});
            skLineSegment(sketch, "E279", {"start": v(532.55, -858.4) * mm, "end": v(491.67, -881.33) * mm});
            skLineSegment(sketch, "E280", {"start": v(491.67, -881.33) * mm, "end": v(563.84, -870.14) * mm});
            skLineSegment(sketch, "E281", {"start": v(532.55, -858.4) * mm, "end": v(532.55, -874.52) * mm});
            skLineSegment(sketch, "E282", {"start": v(474.57, -863.03) * mm, "end": v(426.95, -867.8) * mm});
            skPoint(sketch, "E282.endSnap0", {"position": v(474.57, -867.8) * mm});
            skPoint(sketch, "E283.endSnap0", {"position": v(753.07, -885.64) * mm});
            skLineSegment(sketch, "E284", {"start": v(769.85, -865.76) * mm, "end": v(769.61, -865.82) * mm});
            skLineSegment(sketch, "E285", {"start": v(426.95, -835.27) * mm, "end": v(539.18, -835.27) * mm});
            skLineSegment(sketch, "E286", {"start": v(769.85, -835.27) * mm, "end": v(746.75, -835.27) * mm});
            skLineSegment(sketch, "E287", {"start": v(754.8, -867.82) * mm, "end": v(769.61, -865.82) * mm});
            skLineSegment(sketch, "E288", {"start": v(675.37, -792.92) * mm, "end": v(676.34, -791.77) * mm});
            skPoint(sketch, "E289.start.orphan", {"position": v(579.84, -835.27) * mm});
            skLineSegment(sketch, "E290.bottom", {"start": v(-409.68, -873.3) * mm, "end": v(-66.78, -873.3) * mm});
            skLineSegment(sketch, "E290.top", {"start": v(-409.68, -1216.2) * mm, "end": v(-66.78, -1216.2) * mm});
            skLineSegment(sketch, "E290.left", {"start": v(-409.68, -873.3) * mm, "end": v(-409.68, -1216.2) * mm});
            skLineSegment(sketch, "E290.right", {"start": v(-66.78, -873.3) * mm, "end": v(-66.78, -1216.2) * mm});
            skPoint(sketch, "E290.middle", {"position": v(-216.48, -1127.3) * mm});
            skLineSegment(sketch, "E291", {"start": v(-136.13, -1196.36) * mm, "end": v(-159.42, -1046.2) * mm});
            skLineSegment(sketch, "E292", {"start": v(-159.73, -1045.6) * mm, "end": v(-196.2, -1185.47) * mm});
            skLineSegment(sketch, "E293", {"start": v(-159.86, -1045.37) * mm, "end": v(-251.68, -1149.62) * mm});
            skLineSegment(sketch, "E294", {"start": v(-159.95, -1045.2) * mm, "end": v(-293.9, -1096.2) * mm});
            skLineSegment(sketch, "E295", {"start": v(-158.33, -1047.14) * mm, "end": v(-86.2, -1165.53) * mm});
            skLineSegment(sketch, "E296", {"start": v(-157.76, -1046.6) * mm, "end": v(-80.92, -1111.3) * mm});
            skLineSegment(sketch, "E297", {"start": v(-157.32, -1046.09) * mm, "end": v(-95.99, -1073.6) * mm});
            skLineSegment(sketch, "E298", {"start": v(-150.66, -1034.45) * mm, "end": v(-139.08, -1020.7) * mm});
            skLineSegment(sketch, "E299", {"start": v(-156.48, -1045.1) * mm, "end": v(-115.1, -1045.5) * mm});
            skLineSegment(sketch, "E300", {"start": v(-160.32, -1044.48) * mm, "end": v(-246.84, -975.53) * mm});
            skLineSegment(sketch, "E301", {"start": v(-160.1, -1044.9) * mm, "end": v(-298.4, -1000.32) * mm});
            skLineSegment(sketch, "E302", {"start": v(-161.95, -1041.38) * mm, "end": v(-198.52, -984.33) * mm});
            skLineSegment(sketch, "E303", {"start": v(-159.6, -1039.95) * mm, "end": v(-159.6, -1004.75) * mm});
            skLineSegment(sketch, "E304", {"start": v(-155.44, -1043.86) * mm, "end": v(-124.42, -1034.86) * mm});
            skPoint(sketch, "E304.endSnap0", {"position": v(-151.6, -1034.86) * mm});
            skLineSegment(sketch, "E305", {"start": v(-124.42, -1034.86) * mm, "end": v(-124.42, -1034.86) * mm});
            skLineSegment(sketch, "E306", {"start": v(-115.1, -1045.5) * mm, "end": v(-115.1, -1045.5) * mm});
            skLineSegment(sketch, "E307", {"start": v(-95.99, -1073.6) * mm, "end": v(-94.8, -1075.78) * mm});
            skLineSegment(sketch, "E308", {"start": v(-251.68, -1149.62) * mm, "end": v(-251.68, -1149.62) * mm});
            skLineSegment(sketch, "E309", {"start": v(-248.86, -1151.45) * mm, "end": v(-249.18, -1151.84) * mm});
            skLineSegment(sketch, "E310.0", {"start": v(-250.2, -1150.58) * mm, "end": v(-261.94, -1164.52) * mm});
            skLineSegment(sketch, "E311.0", {"start": v(-247.51, -1152.32) * mm, "end": v(-259.25, -1166.26) * mm});
            skLineSegment(sketch, "E312", {"start": v(-261.94, -1164.52) * mm, "end": v(-259.25, -1166.26) * mm});
            skLineSegment(sketch, "E313", {"start": v(-160.02, -1045.06) * mm, "end": v(-309.58, -1045.06) * mm});
            skLineSegment(sketch, "E314", {"start": v(-161.95, -1041.38) * mm, "end": v(-150.69, -1034.52) * mm});
            skLineSegment(sketch, "E315", {"start": v(-161.95, -1041.38) * mm, "end": v(-158.65, -1047.66) * mm});
            skLineSegment(sketch, "E316", {"start": v(-158.65, -1047.66) * mm, "end": v(-150.69, -1034.52) * mm});
            skLineSegment(sketch, "E317", {"start": v(-158.65, -1047.66) * mm, "end": v(-153.35, -1041.38) * mm});
            skLineSegment(sketch, "E318", {"start": v(-153.35, -1041.38) * mm, "end": v(-150.69, -1034.52) * mm});
            skPoint(sketch, "E319.orphan", {"position": v(-159.6, -1045.06) * mm});
            skLineSegment(sketch, "E320", {"start": v(-246.84, -975.53) * mm, "end": v(-298.4, -1000.32) * mm});
            skLineSegment(sketch, "E321", {"start": v(-298.4, -1000.32) * mm, "end": v(-309.58, -1045.06) * mm});
            skLineSegment(sketch, "E322", {"start": v(-309.58, -1045.06) * mm, "end": v(-293.9, -1096.2) * mm});
            skLineSegment(sketch, "E323", {"start": v(-293.9, -1096.2) * mm, "end": v(-251.68, -1149.62) * mm});
            skLineSegment(sketch, "E324", {"start": v(-251.68, -1149.62) * mm, "end": v(-196.2, -1185.47) * mm});
            skLineSegment(sketch, "E325", {"start": v(-196.2, -1185.47) * mm, "end": v(-136.13, -1196.36) * mm});
            skLineSegment(sketch, "E326", {"start": v(-86.2, -1165.53) * mm, "end": v(-136.13, -1196.36) * mm});
            skLineSegment(sketch, "E327", {"start": v(-86.2, -1165.53) * mm, "end": v(-80.92, -1111.3) * mm});
            skLineSegment(sketch, "E328", {"start": v(-80.92, -1111.3) * mm, "end": v(-95.99, -1073.6) * mm});
            skLineSegment(sketch, "E329", {"start": v(-115.1, -1045.5) * mm, "end": v(-95.99, -1073.6) * mm});
            skLineSegment(sketch, "E330", {"start": v(-124.42, -1034.86) * mm, "end": v(-115.1, -1045.5) * mm});
            skLineSegment(sketch, "E331", {"start": v(-139.08, -1020.7) * mm, "end": v(-124.42, -1034.86) * mm});
            skLineSegment(sketch, "E332", {"start": v(-246.84, -975.53) * mm, "end": v(-198.52, -984.33) * mm});
            skLineSegment(sketch, "E333", {"start": v(-198.52, -984.33) * mm, "end": v(-159.6, -1004.75) * mm});
            skLineSegment(sketch, "E334", {"start": v(-159.6, -1004.75) * mm, "end": v(-139.08, -1020.7) * mm});
            skPoint(sketch, "E335.endSnap0", {"position": v(-83.56, -1138.41) * mm});
            skLineSegment(sketch, "E336", {"start": v(-66.78, -1118.54) * mm, "end": v(-67.02, -1118.6) * mm});
            skLineSegment(sketch, "E337", {"start": v(-409.68, -1088.04) * mm, "end": v(-297.45, -1088.04) * mm});
            skLineSegment(sketch, "E338", {"start": v(-66.78, -1088.04) * mm, "end": v(-89.87, -1088.04) * mm});
            skLineSegment(sketch, "E339", {"start": v(-161.26, -1045.7) * mm, "end": v(-160.3, -1044.54) * mm});
            skPoint(sketch, "E340.start.orphan", {"position": v(-256.8, -1088.04) * mm});
            skLineSegment(sketch, "E341", {"start": v(-206.7, -646.78) * mm, "end": v(-217.31, -663.2) * mm});
            skLineSegment(sketch, "E342", {"start": v(-217.31, -663.2) * mm, "end": v(-221.75, -660.34) * mm});
            skLineSegment(sketch, "E343", {"start": v(-221.75, -660.34) * mm, "end": v(-209.8, -644.76) * mm});
            skPoint(sketch, "E344.trimOffspring.end.orphan", {"position": v(-47.75, 38.5) * mm});
            skLineSegment(sketch, "E345.bottom", {"start": v(-1259.2, -456.62) * mm, "end": v(-916.3, -456.62) * mm});
            skLineSegment(sketch, "E345.top", {"start": v(-1259.2, -799.52) * mm, "end": v(-916.3, -799.52) * mm});
            skLineSegment(sketch, "E345.left", {"start": v(-1259.2, -456.62) * mm, "end": v(-1259.2, -799.52) * mm});
            skLineSegment(sketch, "E345.right", {"start": v(-916.3, -456.62) * mm, "end": v(-916.3, -799.52) * mm});
            skPoint(sketch, "E345.middle", {"position": v(-1087.75, -710.62) * mm});
            skEllipse(sketch, "E346", {"center": v(-1071.1, -670.96) * mm, "majorRadius": 135.13 * mm, "minorRadius": 85.6 * mm, "majorAxis": v(0.74, -0.67), "construction": true});
            skLineSegment(sketch, "E347", {"start": v(-1005.47, -780.12) * mm, "end": v(-1035.2, -626) * mm});
            skLineSegment(sketch, "E348", {"start": v(-1035.2, -626) * mm, "end": v(-1064.16, -773.75) * mm});
            skLineSegment(sketch, "E349", {"start": v(-1035.2, -626) * mm, "end": v(-1128.5, -734.46) * mm});
            skLineSegment(sketch, "E350", {"start": v(-1035.2, -626) * mm, "end": v(-1171.17, -680.17) * mm});
            skLineSegment(sketch, "E351", {"start": v(-1035.2, -626) * mm, "end": v(-1185.66, -611.5) * mm});
            skLineSegment(sketch, "E352", {"start": v(-1035.2, -626) * mm, "end": v(-1152.39, -566.68) * mm});
            skLineSegment(sketch, "E353", {"start": v(-1035.2, -626) * mm, "end": v(-1095.72, -563.09) * mm});
            skLineSegment(sketch, "E354", {"start": v(-1035.2, -626) * mm, "end": v(-960.21, -744.22) * mm});
            skLineSegment(sketch, "E355", {"start": v(-1035.2, -626) * mm, "end": v(-959.93, -689.06) * mm});
            skLineSegment(sketch, "E356", {"start": v(-1035.2, -626) * mm, "end": v(-977.74, -650.05) * mm});
            skLineSegment(sketch, "E357", {"start": v(-1035.2, -626) * mm, "end": v(-1017.13, -604.43) * mm});
            skLineSegment(sketch, "E358", {"start": v(-1035.2, -626) * mm, "end": v(-1010.55, -610.36) * mm});
            skLineSegment(sketch, "E359", {"start": v(-1035.2, -626) * mm, "end": v(-985.7, -638.33) * mm});
            skLineSegment(sketch, "E360", {"start": v(-1035.2, -626) * mm, "end": v(-967.42, -669.08) * mm});
            skLineSegment(sketch, "E361", {"start": v(-1035.2, -626) * mm, "end": v(-955.59, -717.5) * mm});
            skLineSegment(sketch, "E362", {"start": v(-1035.2, -626) * mm, "end": v(-1123.66, -560.37) * mm});
            skLineSegment(sketch, "E363", {"start": v(-1035.2, -626) * mm, "end": v(-1175.21, -585.16) * mm});
            skLineSegment(sketch, "E364", {"start": v(-1035.2, -626) * mm, "end": v(-1184.2, -645.14) * mm});
            skLineSegment(sketch, "E365", {"start": v(-1035.2, -626) * mm, "end": v(-1151.07, -710.62) * mm});
            skLineSegment(sketch, "E366", {"start": v(-1035.2, -626) * mm, "end": v(-1100.8, -755.62) * mm});
            skLineSegment(sketch, "E367", {"start": v(-1035.2, -626) * mm, "end": v(-1035.2, -780.78) * mm});
            skLineSegment(sketch, "E368", {"start": v(-1035.2, -626) * mm, "end": v(-978.42, -768.52) * mm});
            skLineSegment(sketch, "E369", {"start": v(-1035.2, -626) * mm, "end": v(-1065.89, -573.05) * mm});
            skLineSegment(sketch, "E370", {"start": v(-1035.2, -626) * mm, "end": v(-1048.47, -581.99) * mm});
            skLineSegment(sketch, "E371", {"start": v(-1035.2, -626) * mm, "end": v(-1035.2, -590.41) * mm});
            skLineSegment(sketch, "E372", {"start": v(-1035.2, -626) * mm, "end": v(-1026.64, -596.66) * mm});
            skLineSegment(sketch, "E373", {"start": v(-1035.2, -626) * mm, "end": v(-1002.67, -618.18) * mm});
            skPoint(sketch, "E373.endSnap0", {"position": v(-1022.88, -618.18) * mm});
            skLineSegment(sketch, "E374", {"start": v(-1035.2, -626) * mm, "end": v(-995.56, -626) * mm});
            skLineSegment(sketch, "E375", {"start": v(-1035.2, -626) * mm, "end": v(-1071.1, -670.96) * mm, "construction": true});
            skLineSegment(sketch, "E376", {"start": v(-1185.66, -611.5) * mm, "end": v(-1175.21, -585.16) * mm});
            skLineSegment(sketch, "E377", {"start": v(-1175.21, -585.16) * mm, "end": v(-1152.39, -566.68) * mm});
            skLineSegment(sketch, "E378", {"start": v(-1152.39, -566.68) * mm, "end": v(-1123.66, -560.37) * mm});
            skLineSegment(sketch, "E379", {"start": v(-1123.66, -560.37) * mm, "end": v(-1095.72, -563.09) * mm});
            skLineSegment(sketch, "E380", {"start": v(-1095.72, -563.09) * mm, "end": v(-1065.89, -573.05) * mm});
            skLineSegment(sketch, "E381", {"start": v(-1065.89, -573.05) * mm, "end": v(-1048.47, -581.99) * mm});
            skLineSegment(sketch, "E382", {"start": v(-1048.47, -581.99) * mm, "end": v(-1035.2, -590.41) * mm});
            skLineSegment(sketch, "E383", {"start": v(-1035.2, -590.41) * mm, "end": v(-1026.64, -596.66) * mm});
            skLineSegment(sketch, "E384", {"start": v(-1026.64, -596.66) * mm, "end": v(-1017.13, -604.43) * mm});
            skLineSegment(sketch, "E385", {"start": v(-1017.13, -604.43) * mm, "end": v(-1010.55, -610.36) * mm});
            skLineSegment(sketch, "E386", {"start": v(-1010.55, -610.36) * mm, "end": v(-1002.67, -618.18) * mm});
            skLineSegment(sketch, "E387", {"start": v(-1002.67, -618.18) * mm, "end": v(-995.56, -626) * mm});
            skLineSegment(sketch, "E388", {"start": v(-995.56, -626) * mm, "end": v(-985.7, -638.33) * mm});
            skLineSegment(sketch, "E389", {"start": v(-985.7, -638.33) * mm, "end": v(-977.74, -650.05) * mm});
            skLineSegment(sketch, "E390", {"start": v(-977.74, -650.05) * mm, "end": v(-967.42, -669.08) * mm});
            skLineSegment(sketch, "E391", {"start": v(-967.42, -669.08) * mm, "end": v(-959.93, -689.06) * mm});
            skLineSegment(sketch, "E392", {"start": v(-959.93, -689.06) * mm, "end": v(-955.59, -717.5) * mm});
            skLineSegment(sketch, "E393", {"start": v(-955.59, -717.5) * mm, "end": v(-960.21, -744.22) * mm});
            skLineSegment(sketch, "E394", {"start": v(-960.21, -744.22) * mm, "end": v(-978.42, -768.52) * mm});
            skLineSegment(sketch, "E395", {"start": v(-978.42, -768.52) * mm, "end": v(-1005.47, -780.12) * mm});
            skLineSegment(sketch, "E396", {"start": v(-1005.47, -780.12) * mm, "end": v(-1035.2, -780.78) * mm});
            skLineSegment(sketch, "E397", {"start": v(-1035.2, -780.78) * mm, "end": v(-1064.16, -773.75) * mm});
            skLineSegment(sketch, "E398", {"start": v(-1064.16, -773.75) * mm, "end": v(-1100.8, -755.62) * mm});
            skLineSegment(sketch, "E399", {"start": v(-1100.8, -755.62) * mm, "end": v(-1128.5, -734.46) * mm});
            skLineSegment(sketch, "E400", {"start": v(-1128.5, -734.46) * mm, "end": v(-1151.07, -710.62) * mm});
            skLineSegment(sketch, "E401", {"start": v(-1151.07, -710.62) * mm, "end": v(-1171.17, -680.17) * mm});
            skLineSegment(sketch, "E402", {"start": v(-1171.17, -680.17) * mm, "end": v(-1184.2, -645.14) * mm});
            skLineSegment(sketch, "E403", {"start": v(-1184.2, -645.14) * mm, "end": v(-1185.66, -611.5) * mm});
            skLineSegment(sketch, "E404", {"start": v(-1124.32, -737.65) * mm, "end": v(-1124.55, -737.94) * mm});
            skLineSegment(sketch, "E405.0", {"start": v(-1125.58, -736.68) * mm, "end": v(-1145.8, -762.02) * mm});
            skLineSegment(sketch, "E406.0", {"start": v(-1123.06, -738.61) * mm, "end": v(-1143.33, -764) * mm});
            skLineSegment(sketch, "E407", {"start": v(-1259.2, -613.18) * mm, "end": v(-1185.6, -613.18) * mm});
            skLineSegment(sketch, "E408", {"start": v(-1185.6, -613.18) * mm, "end": v(-1007.7, -613.18) * mm, "construction": true});
            skLineSegment(sketch, "E409", {"start": v(-1007.7, -613.18) * mm, "end": v(-916.3, -613.18) * mm});
            skLineSegment(sketch, "E410", {"start": v(-1145.8, -762.02) * mm, "end": v(-1143.33, -764) * mm});
            skLineSegment(sketch, "E411.bottom", {"start": v(359.49, 443.24) * mm, "end": v(702.39, 443.24) * mm});
            skLineSegment(sketch, "E411.top", {"start": v(359.49, 100.34) * mm, "end": v(702.39, 100.34) * mm});
            skLineSegment(sketch, "E411.left", {"start": v(359.49, 443.24) * mm, "end": v(359.49, 100.34) * mm});
            skLineSegment(sketch, "E411.right", {"start": v(702.39, 443.24) * mm, "end": v(702.39, 100.34) * mm});
            skPoint(sketch, "E411.middle", {"position": v(530.94, 271.79) * mm});
            skEllipse(sketch, "E412", {"center": v(540.68, 297.03) * mm, "majorRadius": 173.42 * mm, "minorRadius": 115.92 * mm, "majorAxis": v(-0.82, 0.58)});
            skSolve(sketch);
        }
        {
            var Q0;
            {var subQ8=sQuery(id+"F0.wireOp",EDGE,"E0.top");Q0=makeQuery(id+"F0.imprint","IMPRINT",FACE,{"disambiguationData":[TD([[makeQuery(id+"F0.imprint","IMPRINT",EDGE,{"derivedFrom":subQ8}),1.0]])]});}
            var Q1;
            {var subQ0=sQuery(id+"F0.wireOp",EDGE,"E116");Q1=makeQuery(id+"F0.imprint","IMPRINT",FACE,{"disambiguationData":[TD([[makeQuery(id+"F0.imprint","IMPRINT",EDGE,{"derivedFrom":subQ0}),1.0]])]});}
            var Q2;
            {var subQ3=sQuery(id+"F0.wireOp",EDGE,"E119");Q2=makeQuery(id+"F0.imprint","IMPRINT",FACE,{"disambiguationData":[TD([[makeQuery(id+"F0.imprint","IMPRINT",EDGE,{"derivedFrom":subQ3}),-1.0]])]});}
            var Q3;
            {var subQ4=sQuery(id+"F0.wireOp",EDGE,"E122.trimOffspring");Q3=makeQuery(id+"F0.imprint","IMPRINT",FACE,{"disambiguationData":[TD([[makeQuery(id+"F0.imprint","IMPRINT",EDGE,{"derivedFrom":subQ4}),-1.0]])]});}
            var Q4;
            {var subQ4=sQuery(id+"F0.wireOp",EDGE,"E101");Q4=makeQuery(id+"F0.imprint","IMPRINT",FACE,{"disambiguationData":[TD([[makeQuery(id+"F0.imprint","IMPRINT",EDGE,{"derivedFrom":subQ4}),1.0]])]});}
            extrude(context, id + "F1", {"entities" : qUnion([Q0, Q1, Q2, Q3, Q4]), "depth" : 25.4 * mm, "offsetDistance" : 25.4 * mm});
        }
        {
            var Q0;
            {var subQ0=sQuery(id+"F0.wireOp",EDGE,"E108");Q0=makeQuery(id+"F0.imprint","IMPRINT",FACE,{"disambiguationData":[TD([[makeQuery(id+"F0.imprint","IMPRINT",EDGE,{"derivedFrom":subQ0}),1.0]])]});}
            var Q1;
            {var subQ0=sQuery(id+"F0.wireOp",EDGE,"E119");Q1=makeQuery(id+"F0.imprint","IMPRINT",FACE,{"disambiguationData":[TD([[makeQuery(id+"F0.imprint","IMPRINT",EDGE,{"derivedFrom":subQ0}),1.0]])]});}
            var Q2;
            {var subQ4=sQuery(id+"F0.wireOp",EDGE,"E121.trimOffspring");Q2=makeQuery(id+"F0.imprint","IMPRINT",FACE,{"disambiguationData":[TD([[makeQuery(id+"F0.imprint","IMPRINT",EDGE,{"derivedFrom":subQ4}),-1.0]])]});}
            var Q3;
            {var subQ3=sQuery(id+"F0.wireOp",EDGE,"E123.trimOffspring");Q3=makeQuery(id+"F0.imprint","IMPRINT",FACE,{"disambiguationData":[TD([[makeQuery(id+"F0.imprint","IMPRINT",EDGE,{"derivedFrom":subQ3}),-1.0]])]});}
            var Q4;
            {var subQ4=sQuery(id+"F0.wireOp",EDGE,"E117");Q4=makeQuery(id+"F0.imprint","IMPRINT",FACE,{"disambiguationData":[TD([[makeQuery(id+"F0.imprint","IMPRINT",EDGE,{"derivedFrom":subQ4}),-1.0]])]});}
            var Q5;
            {var subQ9=sQuery(id+"F0.wireOp",EDGE,"E85");var subQ11=makeQuery(id+"F0.imprint","INTERSECT",VERTEX,{"derivedFrom":[sQuery(id+"F0.wireOp",EDGE,"E13"),subQ9]});Q5=makeQuery(id+"F0.imprint","IMPRINT",FACE,{"disambiguationData":[TD([[makeQuery(id+"F0.imprint","IMPRINT",EDGE,{"disambiguationData":[TD([[subQ11,-1.0]])],"derivedFrom":subQ9}),-1.0]])]});}
            var Q6;
            {var subQ0=sQuery(id+"F0.wireOp",EDGE,"0f757e35-7127-4d88-8907-ba3f37b80792.0");Q6=makeQuery(id+"F0.imprint","IMPRINT",FACE,{"disambiguationData":[TD([[makeQuery(id+"F0.imprint","IMPRINT",EDGE,{"derivedFrom":subQ0}),1.0]])]});}
            extrude(context, id + "F2", {"entities" : qUnion([Q0, Q1, Q2, Q3, Q4, Q5, Q6]), "depth" : 25.4 * mm, "offsetDistance" : 25.4 * mm});
        }
        {
            var Q0;
            {var subQ0=sQuery(id+"F0.wireOp",EDGE,"E107");Q0=makeQuery(id+"F0.imprint","IMPRINT",FACE,{"disambiguationData":[TD([[makeQuery(id+"F0.imprint","IMPRINT",EDGE,{"derivedFrom":subQ0}),-1.0]])]});}
            var Q1;
            {var subQ0=sQuery(id+"F0.wireOp",EDGE,"E110");Q1=makeQuery(id+"F0.imprint","IMPRINT",FACE,{"disambiguationData":[TD([[makeQuery(id+"F0.imprint","IMPRINT",EDGE,{"derivedFrom":subQ0}),1.0]])]});}
            var Q2;
            {var subQ4=sQuery(id+"F0.wireOp",EDGE,"E115");Q2=makeQuery(id+"F0.imprint","IMPRINT",FACE,{"disambiguationData":[TD([[makeQuery(id+"F0.imprint","IMPRINT",EDGE,{"derivedFrom":subQ4}),-1.0]])]});}
            var Q3;
            {var subQ6=sQuery(id+"F0.wireOp",EDGE,"E89");Q3=makeQuery(id+"F0.imprint","IMPRINT",FACE,{"disambiguationData":[TD([[makeQuery(id+"F0.imprint","IMPRINT",EDGE,{"derivedFrom":subQ6}),1.0]])]});}
            var Q4;
            {var subQ4=sQuery(id+"F0.wireOp",EDGE,"E4");Q4=makeQuery(id+"F0.imprint","IMPRINT",FACE,{"disambiguationData":[TD([[makeQuery(id+"F0.imprint","IMPRINT",EDGE,{"derivedFrom":subQ4}),-1.0]])]});}
            var Q5;
            {var subQ1=sQuery(id+"F0.wireOp",EDGE,"E10");Q5=makeQuery(id+"F0.imprint","IMPRINT",FACE,{"disambiguationData":[TD([[makeQuery(id+"F0.imprint","IMPRINT",EDGE,{"derivedFrom":subQ1}),1.0]])]});}
            var Q6;
            {var subQ1=sQuery(id+"F0.wireOp",EDGE,"E12");Q6=makeQuery(id+"F0.imprint","IMPRINT",FACE,{"disambiguationData":[TD([[makeQuery(id+"F0.imprint","IMPRINT",EDGE,{"derivedFrom":subQ1}),-1.0]])]});}
            var Q7;
            {var subQ5=sQuery(id+"F0.wireOp",EDGE,"E1");Q7=makeQuery(id+"F0.imprint","IMPRINT",FACE,{"disambiguationData":[TD([[makeQuery(id+"F0.imprint","IMPRINT",EDGE,{"derivedFrom":subQ5}),-1.0]])]});}
            var Q8;
            {var subQ4=sQuery(id+"F0.wireOp",EDGE,"E2");Q8=makeQuery(id+"F0.imprint","IMPRINT",FACE,{"disambiguationData":[TD([[makeQuery(id+"F0.imprint","IMPRINT",EDGE,{"derivedFrom":subQ4}),-1.0]])]});}
            extrude(context, id + "F3", {"entities" : qUnion([Q0, Q1, Q2, Q3, Q4, Q5, Q6, Q7, Q8]), "depth" : 25.4 * mm, "offsetDistance" : 25.4 * mm});
        }
        {
            var Q0;
            {var subQ4=sQuery(id+"F0.wireOp",EDGE,"E8");Q0=makeQuery(id+"F0.imprint","IMPRINT",FACE,{"disambiguationData":[TD([[makeQuery(id+"F0.imprint","IMPRINT",EDGE,{"derivedFrom":subQ4}),1.0]])]});}
            var Q1;
            {var subQ0=sQuery(id+"F0.wireOp",EDGE,"E9");Q1=makeQuery(id+"F0.imprint","IMPRINT",FACE,{"disambiguationData":[TD([[makeQuery(id+"F0.imprint","IMPRINT",EDGE,{"derivedFrom":subQ0}),1.0]])]});}
            var Q2;
            {var subQ1=sQuery(id+"F0.wireOp",EDGE,"E6");Q2=makeQuery(id+"F0.imprint","IMPRINT",FACE,{"disambiguationData":[TD([[makeQuery(id+"F0.imprint","IMPRINT",EDGE,{"derivedFrom":subQ1}),1.0]])]});}
            var Q3;
            {var subQ0=sQuery(id+"F0.wireOp",EDGE,"E1");Q3=makeQuery(id+"F0.imprint","IMPRINT",FACE,{"disambiguationData":[TD([[makeQuery(id+"F0.imprint","IMPRINT",EDGE,{"derivedFrom":subQ0}),1.0]])]});}
            var Q4;
            {var subQ4=sQuery(id+"F0.wireOp",EDGE,"E3");Q4=makeQuery(id+"F0.imprint","IMPRINT",FACE,{"disambiguationData":[TD([[makeQuery(id+"F0.imprint","IMPRINT",EDGE,{"derivedFrom":subQ4}),-1.0]])]});}
            var Q5;
            {var subQ1=sQuery(id+"F0.wireOp",EDGE,"E11");Q5=makeQuery(id+"F0.imprint","IMPRINT",FACE,{"disambiguationData":[TD([[makeQuery(id+"F0.imprint","IMPRINT",EDGE,{"derivedFrom":subQ1}),1.0]])]});}
            var Q6;
            {var subQ1=sQuery(id+"F0.wireOp",EDGE,"E10");Q6=makeQuery(id+"F0.imprint","IMPRINT",FACE,{"disambiguationData":[TD([[makeQuery(id+"F0.imprint","IMPRINT",EDGE,{"derivedFrom":subQ1}),-1.0]])]});}
            extrude(context, id + "F4", {"entities" : qUnion([Q0, Q1, Q2, Q3, Q4, Q5, Q6]), "depth" : 25.4 * mm, "offsetDistance" : 25.4 * mm});
        }
        {
            var Q0;
            Q0=makeQuery(id+"F0.imprint","IMPRINT",FACE,{"disambiguationData":[TD([[makeQuery(id+"F0.imprint","IMPRINT",EDGE,{"derivedFrom":sQuery(id+"F0.wireOp",EDGE,"E8")}),-1.0]])]});
            var Q1;
            {var subQ4=sQuery(id+"F0.wireOp",EDGE,"E7");Q1=makeQuery(id+"F0.imprint","IMPRINT",FACE,{"disambiguationData":[TD([[makeQuery(id+"F0.imprint","IMPRINT",EDGE,{"derivedFrom":subQ4}),1.0]])]});}
            var Q2;
            {var subQ5=sQuery(id+"F0.wireOp",EDGE,"E6");Q2=makeQuery(id+"F0.imprint","IMPRINT",FACE,{"disambiguationData":[TD([[makeQuery(id+"F0.imprint","IMPRINT",EDGE,{"derivedFrom":subQ5}),-1.0]])]});}
            extrude(context, id + "F5", {"entities" : qUnion([Q0, Q1, Q2]), "depth" : 25.4 * mm, "offsetDistance" : 25.4 * mm});
        }
        {
            var Q0;
            Q0=makeQuery(id+"F2.opExtrude","CAP_FACE",FACE,{"disambiguationData":[OSD([sQuery(id+"F0.wireOp",EDGE,"E0.right"),sQuery(id+"F0.wireOp",EDGE,"E99"),sQuery(id+"F0.wireOp",EDGE,"E100"),sQuery(id+"F0.wireOp",EDGE,"E117"),sQuery(id+"F0.wireOp",EDGE,"E125.trimOffspring")])],"isStart":false});
            var sketch = newSketch(context, id + "F6", { "sketchPlane" : qUnion([Q0])});
            skLineSegment(sketch, "E413.0", {"start": v(149.7, 254) * mm, "end": v(149.7, -88.9) * mm});
            skLineSegment(sketch, "E414.0", {"start": v(-193.2, -88.9) * mm, "end": v(149.7, -88.9) * mm});
            skLineSegment(sketch, "E415.0", {"start": v(-193.2, 254) * mm, "end": v(-193.2, -88.9) * mm});
            skLineSegment(sketch, "E416.0", {"start": v(-193.2, 254) * mm, "end": v(149.7, 254) * mm});
            skLineSegment(sketch, "E417.0", {"start": v(-186.85, 247.65) * mm, "end": v(143.35, 247.65) * mm});
            skLineSegment(sketch, "E417.1", {"start": v(-186.85, 247.65) * mm, "end": v(-186.85, -82.55) * mm});
            skLineSegment(sketch, "E417.2", {"start": v(-186.85, -82.55) * mm, "end": v(143.35, -82.55) * mm});
            skLineSegment(sketch, "E417.3", {"start": v(143.35, 247.65) * mm, "end": v(143.35, -82.55) * mm});
            skSolve(sketch);
        }
        {
            var Q0;
            {var subQ11=sQuery(id+"F6.wireOp",EDGE,"E414.0");Q0=makeQuery(id+"F6.imprint","IMPRINT",FACE,{"disambiguationData":[TD([[makeQuery(id+"F6.imprint","IMPRINT",EDGE,{"derivedFrom":subQ11}),1.0]])]});}
            var Q1;
            {var subQ0=sQuery(id+"F6.wireOp",EDGE,"E413.0");var subQ1=makeQuery(id+"F2.opExtrude","CAP_EDGE",EDGE,{"disambiguationData":[OSD([sQuery(id+"F0.wireOp",EDGE,"E117")])],"isStart":false});var subQ2=makeQuery(id+"F6.imprint","INTERSECT",VERTEX,{"derivedFrom":[subQ1,subQ0]});Q1=makeQuery(id+"F6.imprint","IMPRINT",FACE,{"disambiguationData":[TD([[makeQuery(id+"F6.imprint","IMPRINT",EDGE,{"disambiguationData":[TD([[subQ2,1.0]])],"derivedFrom":subQ0}),-1.0]])]});}
            extrude(context, id + "F7", {"entities" : qUnion([Q0, Q1]), "oppositeDirection" : true, "depth" : 25.4 * mm, "offsetDistance" : 25.4 * mm});
        }
        {
            var Q0;
            Q0=makeQuery(id+"F7.opExtrude","SWEPT_BODY",BODY,{"disambiguationData":[OSD([sQuery(id+"F6.wireOp",EDGE,"E413.0"),sQuery(id+"F6.wireOp",EDGE,"E414.0"),sQuery(id+"F6.wireOp",EDGE,"E415.0"),sQuery(id+"F6.wireOp",EDGE,"E416.0"),sQuery(id+"F6.wireOp",EDGE,"E417.0"),sQuery(id+"F6.wireOp",EDGE,"E417.1"),sQuery(id+"F6.wireOp",EDGE,"E417.2"),sQuery(id+"F6.wireOp",EDGE,"E417.3")])]});
            var Q1;
            Q1=makeQuery(id+"F1.opExtrude","SWEPT_BODY",BODY,{"disambiguationData":[OSD([sQuery(id+"F0.wireOp",EDGE,"E0.bottom"),sQuery(id+"F0.wireOp",EDGE,"E0.left"),sQuery(id+"F0.wireOp",EDGE,"E91"),sQuery(id+"F0.wireOp",EDGE,"E92"),sQuery(id+"F0.wireOp",EDGE,"E119"),sQuery(id+"F0.wireOp",EDGE,"E121.trimOffspring")])]});
            var Q2;
            Q2=makeQuery(id+"F2.opExtrude","SWEPT_BODY",BODY,{"disambiguationData":[OSD([sQuery(id+"F0.wireOp",EDGE,"E0.bottom"),sQuery(id+"F0.wireOp",EDGE,"E91"),sQuery(id+"F0.wireOp",EDGE,"E103"),sQuery(id+"F0.wireOp",EDGE,"E121.trimOffspring"),sQuery(id+"F0.wireOp",EDGE,"E122.trimOffspring")])]});
            var Q3;
            Q3=makeQuery(id+"F1.opExtrude","SWEPT_BODY",BODY,{"disambiguationData":[OSD([sQuery(id+"F0.wireOp",EDGE,"E0.bottom"),sQuery(id+"F0.wireOp",EDGE,"E103"),sQuery(id+"F0.wireOp",EDGE,"E104"),sQuery(id+"F0.wireOp",EDGE,"E122.trimOffspring"),sQuery(id+"F0.wireOp",EDGE,"E123.trimOffspring")])]});
            var Q4;
            Q4=makeQuery(id+"F2.opExtrude","SWEPT_BODY",BODY,{"disambiguationData":[OSD([sQuery(id+"F0.wireOp",EDGE,"E0.bottom"),sQuery(id+"F0.wireOp",EDGE,"E0.right"),sQuery(id+"F0.wireOp",EDGE,"E104"),sQuery(id+"F0.wireOp",EDGE,"E105"),sQuery(id+"F0.wireOp",EDGE,"E123.trimOffspring"),sQuery(id+"F0.wireOp",EDGE,"E126.trimOffspring")])]});
            var Q5;
            Q5=makeQuery(id+"F1.opExtrude","SWEPT_BODY",BODY,{"disambiguationData":[OSD([sQuery(id+"F0.wireOp",EDGE,"E0.right"),sQuery(id+"F0.wireOp",EDGE,"E100"),sQuery(id+"F0.wireOp",EDGE,"E101"),sQuery(id+"F0.wireOp",EDGE,"E102"),sQuery(id+"F0.wireOp",EDGE,"E105"),sQuery(id+"F0.wireOp",EDGE,"E125.trimOffspring"),sQuery(id+"F0.wireOp",EDGE,"E126.trimOffspring")])]});
            var Q6;
            Q6=makeQuery(id+"F2.opExtrude","SWEPT_BODY",BODY,{"disambiguationData":[OSD([sQuery(id+"F0.wireOp",EDGE,"E0.right"),sQuery(id+"F0.wireOp",EDGE,"E99"),sQuery(id+"F0.wireOp",EDGE,"E100"),sQuery(id+"F0.wireOp",EDGE,"E117"),sQuery(id+"F0.wireOp",EDGE,"E125.trimOffspring")])]});
            var Q7;
            Q7=makeQuery(id+"F2.opExtrude","SWEPT_BODY",BODY,{"disambiguationData":[OSD([sQuery(id+"F0.wireOp",EDGE,"E0.left"),sQuery(id+"F0.wireOp",EDGE,"E92"),sQuery(id+"F0.wireOp",EDGE,"E93"),sQuery(id+"F0.wireOp",EDGE,"E119"),sQuery(id+"F0.wireOp",EDGE,"E120.trimOffspring")])]});
            var Q8;
            Q8=makeQuery(id+"F1.opExtrude","SWEPT_BODY",BODY,{"disambiguationData":[OSD([sQuery(id+"F0.wireOp",EDGE,"E0.left"),sQuery(id+"F0.wireOp",EDGE,"E93"),sQuery(id+"F0.wireOp",EDGE,"E116"),sQuery(id+"F0.wireOp",EDGE,"E120.trimOffspring")])]});
            var Q9;
            Q9=makeQuery(id+"F2.opExtrude","SWEPT_BODY",BODY,{"disambiguationData":[OSD([sQuery(id+"F0.wireOp",EDGE,"E0.left"),sQuery(id+"F0.wireOp",EDGE,"E93"),sQuery(id+"F0.wireOp",EDGE,"E94"),sQuery(id+"F0.wireOp",EDGE,"E106"),sQuery(id+"F0.wireOp",EDGE,"E108"),sQuery(id+"F0.wireOp",EDGE,"E109"),sQuery(id+"F0.wireOp",EDGE,"E111"),sQuery(id+"F0.wireOp",EDGE,"E112"),sQuery(id+"F0.wireOp",EDGE,"E113"),sQuery(id+"F0.wireOp",EDGE,"E116")])]});
            var Q10;
            Q10=makeQuery(id+"F1.opExtrude","SWEPT_BODY",BODY,{"disambiguationData":[OSD([sQuery(id+"F0.wireOp",EDGE,"E0.top"),sQuery(id+"F0.wireOp",EDGE,"E0.left"),sQuery(id+"F0.wireOp",EDGE,"E0.right"),sQuery(id+"F0.wireOp",EDGE,"0f757e35-7127-4d88-8907-ba3f37b80792.0"),sQuery(id+"F0.wireOp",EDGE,"f954dfee-8cd6-48f8-aeed-ad84e5eb6b78.0"),sQuery(id+"F0.wireOp",EDGE,"0mHfBBFU-3LXn-QTQE-vuux-k14rANo4PZTo"),sQuery(id+"F0.wireOp",EDGE,"E94"),sQuery(id+"F0.wireOp",EDGE,"E95"),sQuery(id+"F0.wireOp",EDGE,"E96"),sQuery(id+"F0.wireOp",EDGE,"E97"),sQuery(id+"F0.wireOp",EDGE,"E98"),sQuery(id+"F0.wireOp",EDGE,"E106"),sQuery(id+"F0.wireOp",EDGE,"E107"),sQuery(id+"F0.wireOp",EDGE,"E108"),sQuery(id+"F0.wireOp",EDGE,"E110"),sQuery(id+"F0.wireOp",EDGE,"E111"),sQuery(id+"F0.wireOp",EDGE,"E113"),sQuery(id+"F0.wireOp",EDGE,"E115"),sQuery(id+"F0.wireOp",EDGE,"E118")])]});
            var Q11;
            Q11=makeQuery(id+"F3.opExtrude","SWEPT_BODY",BODY,{"disambiguationData":[OSD([sQuery(id+"F0.wireOp",EDGE,"E0.right"),sQuery(id+"F0.wireOp",EDGE,"E98"),sQuery(id+"F0.wireOp",EDGE,"E99"),sQuery(id+"F0.wireOp",EDGE,"E115"),sQuery(id+"F0.wireOp",EDGE,"E117"),sQuery(id+"F0.wireOp",EDGE,"E118")])]});
            booleanBodies(context, id + "F8", {"operationType" : BooleanOperationType.SUBTRACTION, "tools" : qUnion([Q0]), "targets" : qUnion([Q1, Q2, Q3, Q4, Q5, Q6, Q7, Q8, Q9, Q10, Q11]), "keepTools" : true});
        }
    });
